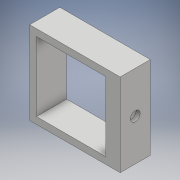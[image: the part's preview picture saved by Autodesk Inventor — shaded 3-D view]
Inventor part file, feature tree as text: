
AUTODESK INVENTOR PART (.ipt)
format: ipt  version: 2018 (Build 220112000, 112)  size: 107,520 bytes
history: native  units: mm
features: extrude x1, hole x1, sketch x1
ambient origin geometry x8: Origin, YZ Plane, XZ Plane, XY Plane, X Axis, Y Axis, Z Axis, Center Point
bodies: Solid1 (feature_tree)
feature tree (3):
  extrude  "Extrusion1"  Depth=46.0mm
  hole  "Hole1"  [1 undecoded]
  sketch  "Sketch1"  dims[d0=46.0mm d1=46.0mm d2=55.0mm d3=55.0mm d4=60.0mm d5=20.0mm d6=0.0mm d7=23.0mm d8=10.0mm d9=6.45mm d10=6.0mm d11=10.525mm d12=6.85mm d13=90.0deg d14=8.0mm d15=20.594885mm]
note: 1 required parameter value undecoded (feature->parameter linkage not recoverable at this tier; creation-order binding heuristic only, values carry confidence <= 0.55)
